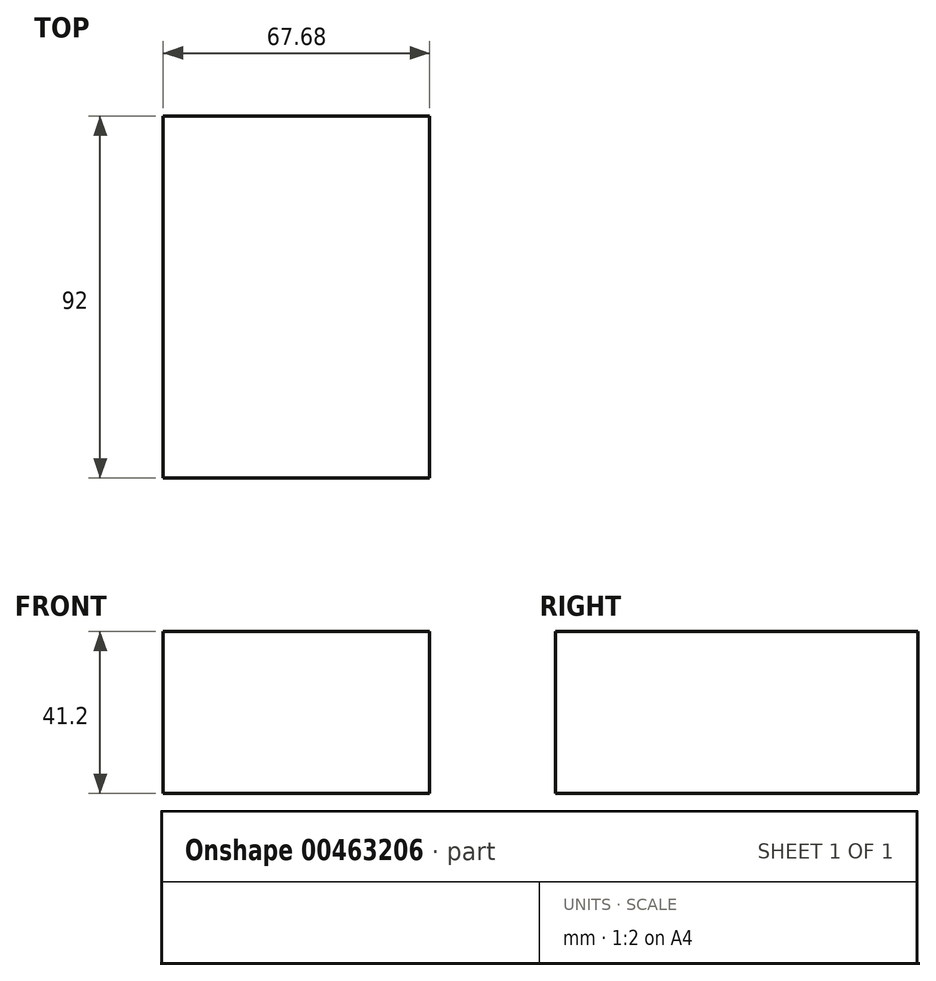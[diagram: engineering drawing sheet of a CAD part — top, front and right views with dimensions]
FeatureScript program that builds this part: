
annotation { "Feature Type Name" : "Feature", "Feature Type Description" : "" }
export const myFeature = defineFeature(function(context is Context, id is Id, definition is map)
    precondition{}
    {
        {
            var Q0;
            Q0=qCreatedBy(makeId("Front.planeOp"),FACE);
            var sketch = newSketch(context, id + "F0", { "sketchPlane" : qUnion([Q0])});
            skLineSegment(sketch, "E0.bottom", {"start": v(-31.28, 15.85) * mm, "end": v(36.4, 15.85) * mm});
            skLineSegment(sketch, "E0.top", {"start": v(-31.28, -25.35) * mm, "end": v(36.4, -25.35) * mm});
            skLineSegment(sketch, "E0.left", {"start": v(-31.28, 15.85) * mm, "end": v(-31.28, -25.35) * mm});
            skLineSegment(sketch, "E0.right", {"start": v(36.4, 15.85) * mm, "end": v(36.4, -25.35) * mm});
            skSolve(sketch);
        }
        {
            var Q0;
            Q0=makeQuery(id+"F0.imprint","IMPRINT",FACE,{"disambiguationData":[TD([[makeQuery(id+"F0.imprint","IMPRINT",EDGE,{"derivedFrom":sQuery(id+"F0.wireOp",EDGE,"E0.bottom")}),-1.0]])]});
            extrude(context, id + "F1", {"entities" : qUnion([Q0]), "depth" : 92 * mm});
        }
    });
